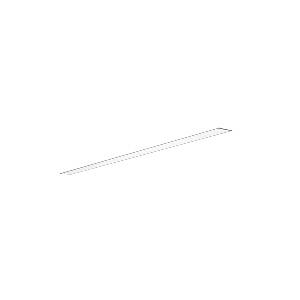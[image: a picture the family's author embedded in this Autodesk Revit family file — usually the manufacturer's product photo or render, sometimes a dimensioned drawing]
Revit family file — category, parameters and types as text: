
# Revit family: dotoo_line_-_dle_1500_840_d_00808223_0a9a
name_source: partatom
category: Lighting Fixtures
units: mm (PartAtom-declared; Revit-internal decimal feet)

## family parameters
Cut with Voids When Loaded = No
Host = Face
Light Source = No
Part Type = Normal
Room Calculation Point = No
Round Connector Dimension = Use Diameter
Shared = No

## types (1)
- DOTOO.line - DLE 1500/840/D (1 x LED, 1350 lm, 4000K)
    Apparent Load = 13 VA
    Approval mark = CE
    CIE Flux Codes = 67 91 98 100 100
    Color Rendering = 80-89
    Color Temperature = 4000K
    Control Gear = Electronic ballast
    Default Elevation = 1800 mm
    Description = DLE 1500/840/D|Recessed luminaire|light source:  |work equipment: Adjustable electronic ballast, digital DALI|connected load: 220-240 V, 50/60 Hz|Power consumption: approx. 13 W|standby: approx. 0,20|power factor: approx. 0,970|luminous flux: 1350 lm|luminous efficacy: 103 lm/W|light distribution: Direct|direct ratio: approx. 100 %|colour temperature: Cold white, ca. 4000 K|color rendering index (CRI): >= 80|chromaticity tolerance:  3 SDCM|System of protection: IP 40|class of protection: I|technology: Continuously dimmable|operation: External|luminaire body|material: Sectional aluminium|colour: White|lamp cover: Acrylic (PMMA), Clear|weight (net): approx. 3.9 kg|mains lead: Connector|Fastening: Fastening bow|glare control: Prism aperture|luminance(L65): <= 3000 cd/m|unified glare rating(4H 8H): <=  19|special features: DALI Load 1x, TouchDIM - dimming via standard switch, Flicker-free, Suitable as emergency lighting|
    Frequency = 50 Hz
    Height = 0 mm  [stored 0 ft]
    Lamp = 1 x LED
    Lamp Light Flux = 1350 lm
    Lamp count = 1
    Length = 1134 mm
    Luminous efficacy = 104 lm/W
    Manufacturer = Waldmann
    ModVariant = No
    Model = 00808223
    Mounting Place = Ceiling
    Mounting Type = Recessed
    Number of Poles = 1
    OnlyDefault = Yes
    Power Factor = 1
    Product Name = DOTOO.line - DLE 1500/840/D
    Product group = Recessed luminaire
    ProductGroupID = 4
    Protection Class = Protection class I
    Protection Degree = IP 40
    RLX_Detail_Level = 1
    RLX_Emergency_Light_Flux = 0 lm
    RLX_Emergency_Type = 0
    RLX_Emergency_Type_DB = No
    RlxData = <blob elided: 13065 chars, md5=fe4911b9>
    Socket = socket
    Standby Power = 0 W
    System Light Flux = 1350 lm
    System Power = 13 W
    Type Comments = Product without accessories
    Type Image = 114405000-00808223.jpg
    URL = http://relux.com
    VarID = ---
    Voltage = 230 V
    Voltage Range = 220-240 V
    Weight = 0.00 kg
    Width = 60 mm  [stored 0.19685 ft]

note: [stored X ft] marks values corroborated as IEEE doubles in the binary element streams (Revit-internal decimal feet)

## geometry (parser evidence)
native form markers: Sweep x9
no freeform markers — native parametric forms only
